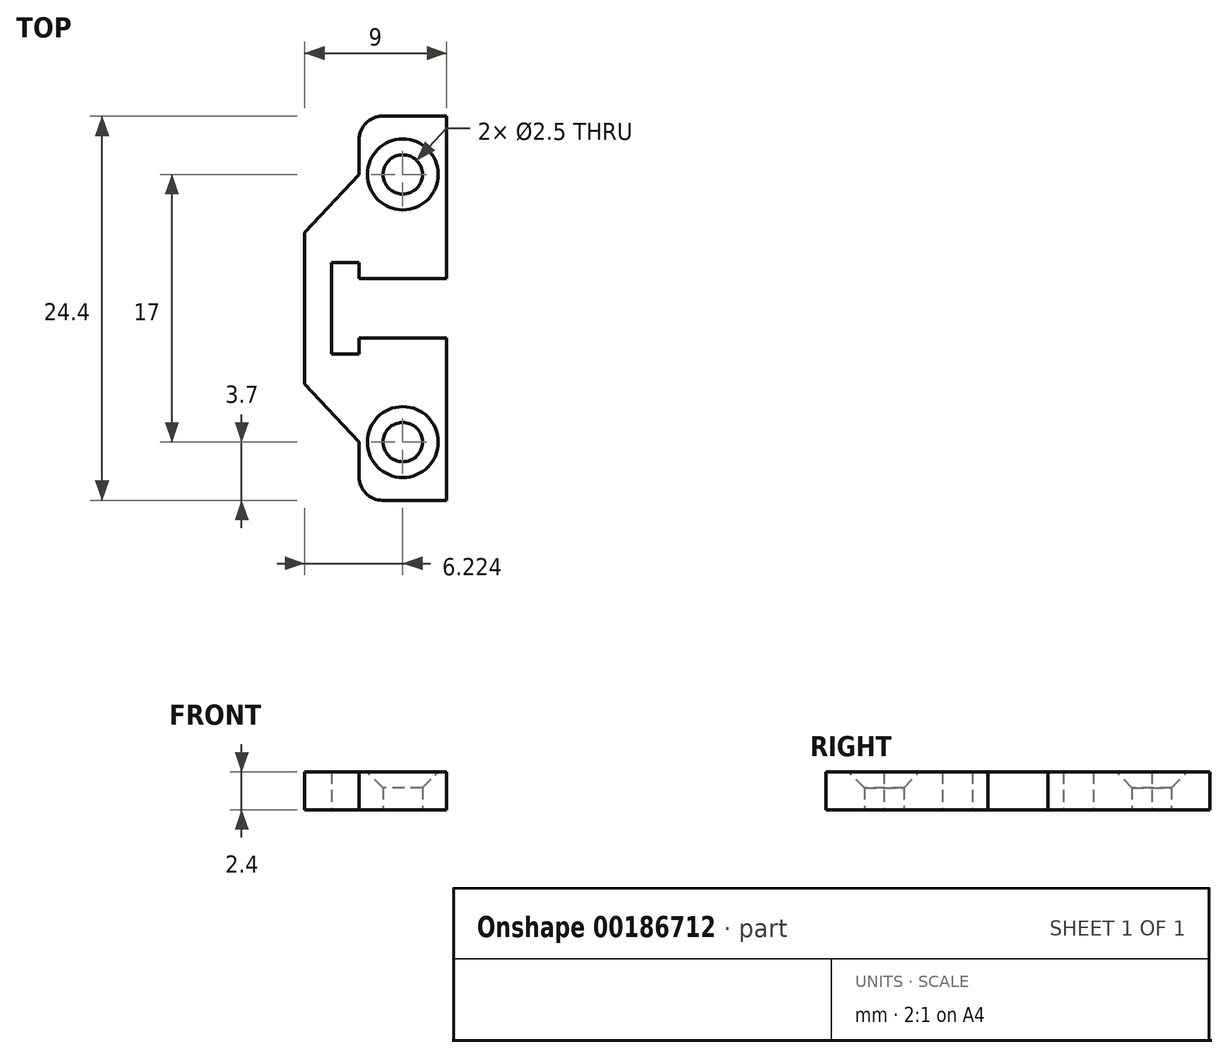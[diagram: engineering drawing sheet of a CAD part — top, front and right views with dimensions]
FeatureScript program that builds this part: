
annotation { "Feature Type Name" : "Feature", "Feature Type Description" : "" }
export const myFeature = defineFeature(function(context is Context, id is Id, definition is map)
    precondition{}
    {
        {
            var Q0;
            Q0=qCreatedBy(makeId("Top.planeOp"),FACE);
            var sketch = newSketch(context, id + "F0", { "sketchPlane" : qUnion([Q0])});
            skCircle(sketch, "E0", {"center": v(1.75, -8.5) * mm, "radius": 1.25 * mm});
            skLineSegment(sketch, "E1.top", {"start": v(4.53, -12.2) * mm, "end": v(0.48, -12.2) * mm});
            skLineSegment(sketch, "E1.left", {"start": v(4.53, -4.8) * mm, "end": v(4.53, -12.2) * mm});
            skLineSegment(sketch, "E1.right", {"start": v(-1.02, -8.5) * mm, "end": v(-1.02, -10.7) * mm});
            skLineSegment(sketch, "E2", {"start": v(-4.47, -4.8) * mm, "end": v(-1.02, -8.5) * mm});
            skLineSegment(sketch, "E3", {"start": v(-1.02, -2.9) * mm, "end": v(-1.02, -1.9) * mm});
            skLineSegment(sketch, "E4", {"start": v(-2.77, -2.9) * mm, "end": v(-1.02, -2.9) * mm});
            skLineSegment(sketch, "E5", {"start": v(-1.02, -1.9) * mm, "end": v(4.53, -1.9) * mm});
            skLineSegment(sketch, "E6", {"start": v(-2.77, -2.9) * mm, "end": v(-2.77, 0) * mm});
            skLineSegment(sketch, "E7", {"start": v(4.53, -1.9) * mm, "end": v(4.53, -4.8) * mm});
            skLineSegment(sketch, "E8", {"start": v(-4.47, -4.8) * mm, "end": v(-4.47, 0) * mm});
            skLineSegment(sketch, "E9.MirrorCS", {"start": v(-1.02, 2.9) * mm, "end": v(-1.02, 1.9) * mm});
            skLineSegment(sketch, "E10.MirrorCS", {"start": v(4.53, 12.2) * mm, "end": v(0.48, 12.2) * mm});
            skLineSegment(sketch, "E11.MirrorCS", {"start": v(-4.47, 4.8) * mm, "end": v(-1.02, 8.5) * mm});
            skPoint(sketch, "E12.MirrorP", {"position": v(1.75, 8.5) * mm});
            skLineSegment(sketch, "E13.MirrorCS", {"start": v(4.53, 4.8) * mm, "end": v(4.53, 12.2) * mm});
            skLineSegment(sketch, "E14.MirrorCS", {"start": v(-4.47, 4.8) * mm, "end": v(-4.47, 0) * mm});
            skLineSegment(sketch, "E15.MirrorCS", {"start": v(-1.02, 8.5) * mm, "end": v(-1.02, 10.7) * mm});
            skLineSegment(sketch, "E16.MirrorCS", {"start": v(-2.77, 2.9) * mm, "end": v(-2.77, 0) * mm});
            skLineSegment(sketch, "E17.MirrorCS", {"start": v(4.53, 1.9) * mm, "end": v(4.53, 4.8) * mm});
            skLineSegment(sketch, "E18.MirrorCS", {"start": v(-2.77, 2.9) * mm, "end": v(-1.02, 2.9) * mm});
            skLineSegment(sketch, "E19.MirrorCS", {"start": v(-1.02, 1.9) * mm, "end": v(4.53, 1.9) * mm});
            skCircle(sketch, "E20.MirrorC", {"center": v(1.75, 8.5) * mm, "radius": 1.25 * mm});
            skLineSegment(sketch, "E21", {"start": v(1.75, -12.2) * mm, "end": v(1.75, 12.2) * mm, "construction": true});
            skPoint(sketch, "E22.visualSharp", {"position": v(-1.02, -12.2) * mm});
            skArc(sketch, "E22.filletArc", {"start": v(-1.02, -10.7) * mm, "mid": v(-0.58, -11.76) * mm, "end": v(0.48, -12.2) * mm});
            skPoint(sketch, "E23.visualSharp", {"position": v(-1.02, 12.2) * mm});
            skArc(sketch, "E23.filletArc", {"start": v(0.48, 12.2) * mm, "mid": v(-0.58, 11.76) * mm, "end": v(-1.02, 10.7) * mm});
            skSolve(sketch);
        }
        {
            var Q0;
            Q0=makeQuery(id+"F0.imprint","IMPRINT",FACE,{"disambiguationData":[TD([[makeQuery(id+"F0.imprint","IMPRINT",EDGE,{"derivedFrom":sQuery(id+"F0.wireOp",EDGE,"E0")}),-1.0]])]});
            extrude(context, id + "F1", {"entities" : qUnion([Q0]), "depth" : 2.4 * mm});
        }
        {
            var Q0;
            Q0=makeQuery(id+"F1.opExtrude","CAP_EDGE",EDGE,{"disambiguationData":[OSD([sQuery(id+"F0.wireOp",EDGE,"E20.MirrorC")])],"isStart":false});
            var Q1;
            Q1=makeQuery(id+"F1.opExtrude","CAP_EDGE",EDGE,{"disambiguationData":[OSD([sQuery(id+"F0.wireOp",EDGE,"E0")])],"isStart":false});
            chamfer(context, id + "F2", {"entities" : qUnion([Q0, Q1]), "width" : 1 * mm, "tangentPropagation" : true});
        }
    });
